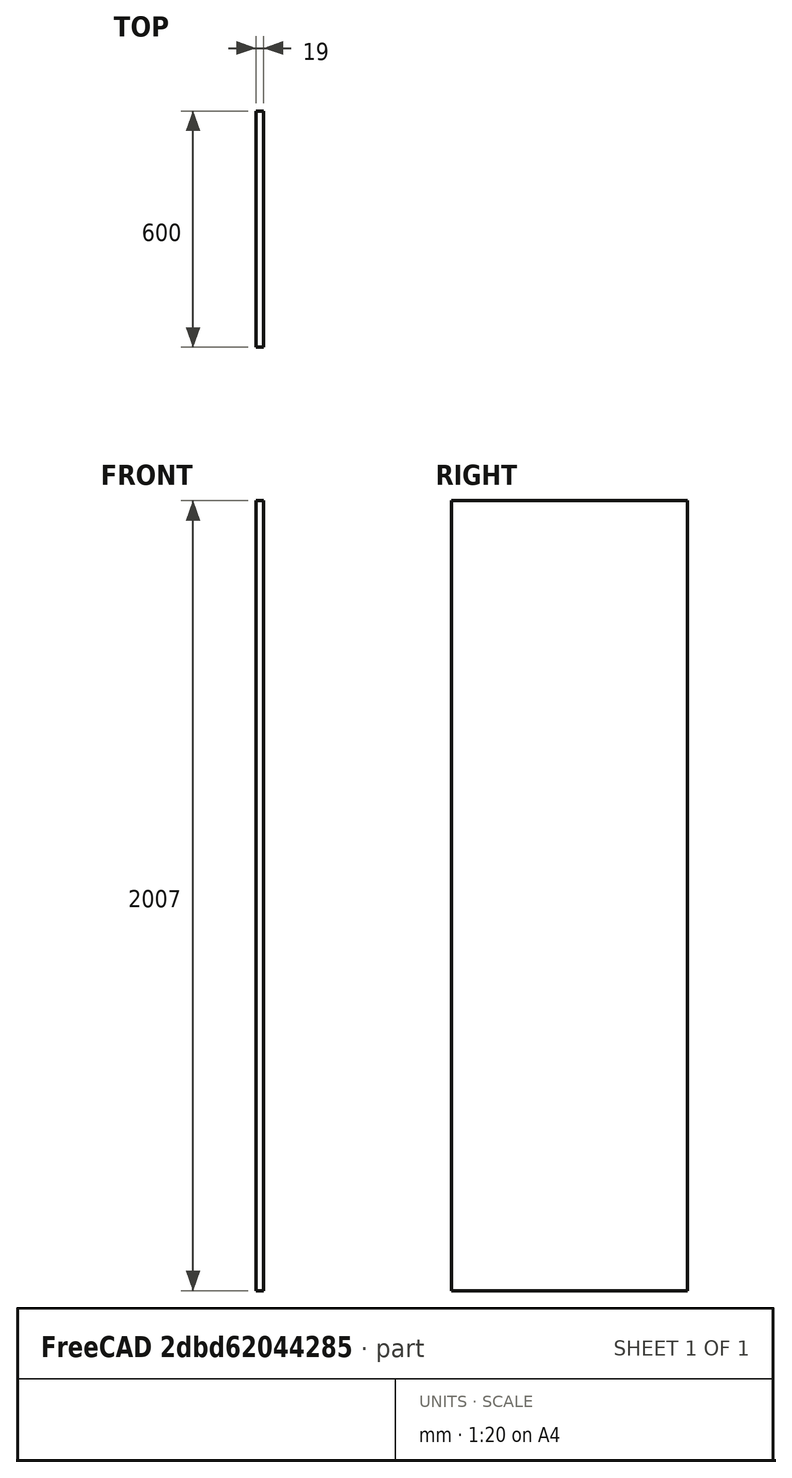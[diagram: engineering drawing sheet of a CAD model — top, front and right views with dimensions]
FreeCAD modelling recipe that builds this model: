
FCSTD DOCUMENT  (FreeCAD 1.0RUnknown)
Label: wardrobe_left_corpus00_jan
License: All rights reserved
LicenseURL: https://en.wikipedia.org/wiki/All_rights_reserved
objects: PartDesign::CoordinateSystem×3, Sketcher::SketchObject×1, PartDesign::Pad×1, PartDesign::Body×1
note: 9 computed .brp shape members not serialized (recipe doc carries the construction recipe); baked Part::Feature solids carry a one-line shape summary decoded from their .brp
EXTERNAL_REF file=../../mastersketch.FCStd obj=Spreadsheet

FEATURE [Sketcher::SketchObject] Sketch001
  ArcFitTolerance = 1e-06
  AttachmentSupport = -> [YZ_Plane001]
  FullyConstrained = true
  MakeInternals = false
  MapMode = 5
  Placement = pos=(0,0,0) rot=(0.57735,0.57735,0.57735;2.0944rad)
  expr: Constraints[10] = mastersketch#Spreadsheet.corpus_depth
  expr: Constraints[11] = mastersketch#Spreadsheet.corpus_height - 2 * mastersketch#Spreadsheet.corpus_outer_thickness
  sketch-geometry (5):
    g0: LineSegment StartX=-300 StartY=-1003.5 StartZ=0 EndX=300 EndY=-1003.5 EndZ=0
    g1: LineSegment StartX=300 StartY=-1003.5 StartZ=0 EndX=300 EndY=1003.5 EndZ=0
    g2: LineSegment StartX=300 StartY=1003.5 StartZ=0 EndX=-300 EndY=1003.5 EndZ=0
    g3: LineSegment StartX=-300 StartY=1003.5 StartZ=0 EndX=-300 EndY=-1003.5 EndZ=0
    g4: GeomPoint [constr] X=0 Y=0 Z=0
  constraints (12):
    c: Coincident(g0,g1)
    c: Coincident(g1,g2)
    c: Coincident(g2,g3)
    c: Coincident(g3,g0)
    c: Horizontal(g0)
    c: Horizontal(g2)
    c: Vertical(g1)
    c: Vertical(g3)
    c: Symmetric(g2,g0,g4)
    c: Coincident(g4,g-1)
    c: DistanceX(g0,g0) = 600
    c: DistanceY(g3,g3) = 2007
FEATURE [PartDesign::Pad] Pad001
  Direction = (1,0,0)
  Length = 19
  Length2 = 10
  Placement = pos=(0,0,0) rot=(1,1,1;2.0944rad)
  Profile = -> Sketch001
  ReferenceAxis = -> Sketch001 [N_Axis]
  Refine = true
  Suppressed = false
  Type = 0
  expr: Length = mastersketch#Spreadsheet.corpus_outer_thickness
FEATURE [PartDesign::CoordinateSystem] LCS_bottom
  AttacherType = Attacher::AttachEngine3D
  AttachmentSupport = -> [Pad001]
  MapMode = 45
  Placement = pos=(0,-1.42e-14,-1003.5) rot=(0,0.707107,0.707107;3.14159rad)
FEATURE [PartDesign::CoordinateSystem] LCS_top
  AttacherType = Attacher::AttachEngine3D
  AttachmentSupport = -> [Pad001]
  MapMode = 45
  Placement = pos=(0,1.42e-14,1003.5) rot=(0,0.707107,0.707107;3.14159rad)
FEATURE [PartDesign::CoordinateSystem] LCS_inner_bottom
  AttacherType = Attacher::AttachEngine3D
  AttachmentSupport = -> [Pad001]
  MapMode = 45
  Placement = pos=(19,-1.82e-14,-1003.5) rot=(0,0.707107,0.707107;3.14159rad)
FEATURE [PartDesign::Body] Body001  label="wardrobe_left_corpus00_jan"
  AllowCompound = false
  Group = -> [Sketch001,Pad001,LCS_bottom,LCS_top,LCS_inner_bottom]
  Origin = -> Origin001
  Tip = -> Pad001
